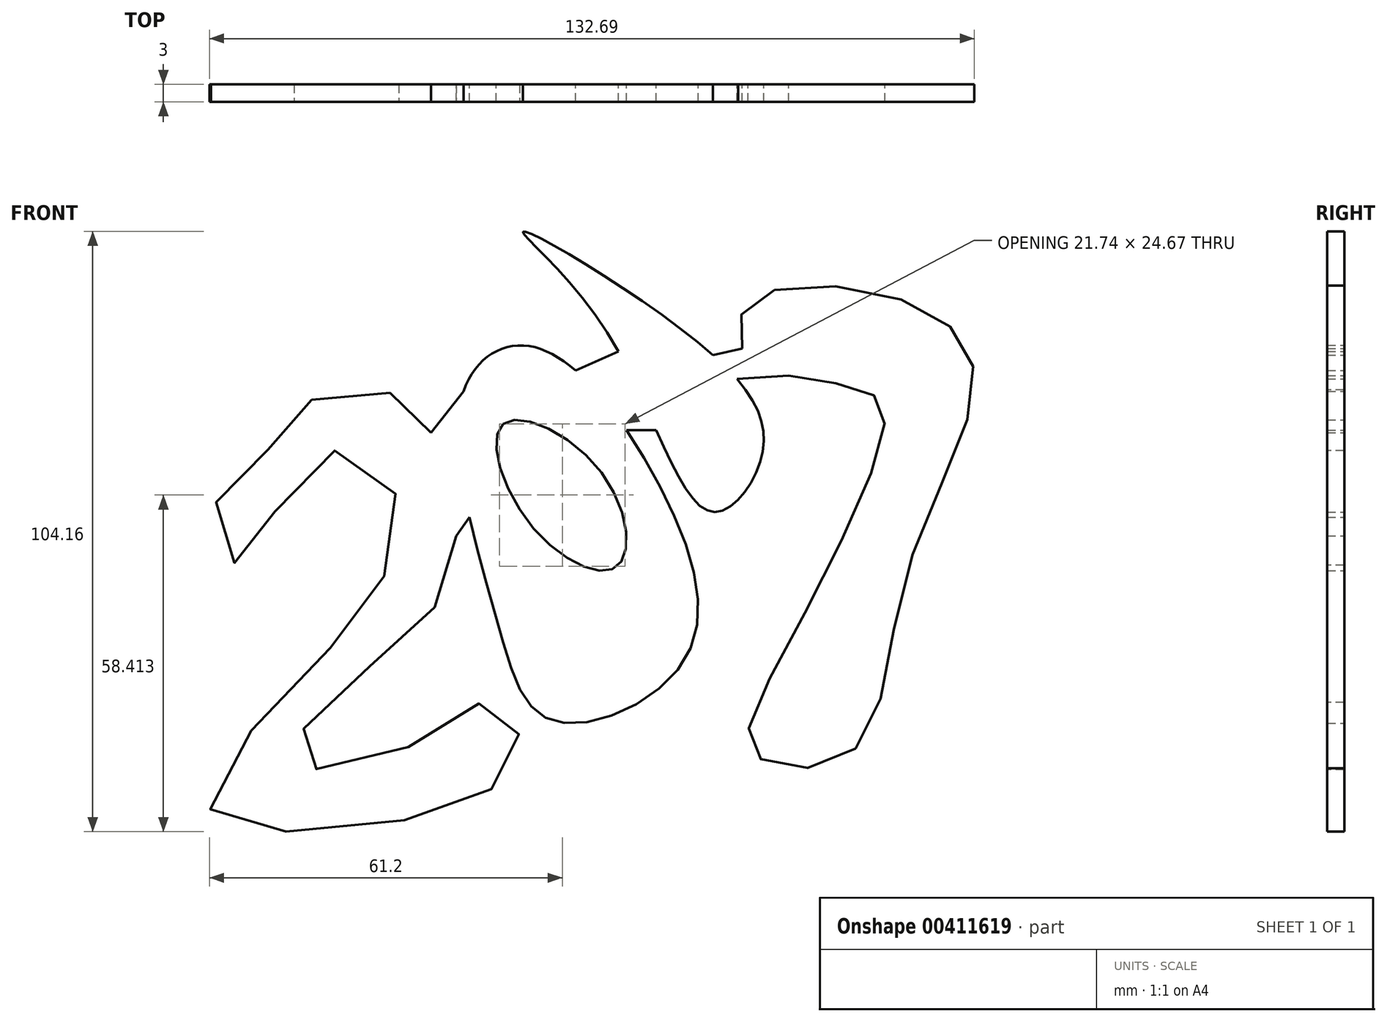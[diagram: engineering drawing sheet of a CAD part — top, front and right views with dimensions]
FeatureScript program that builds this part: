
annotation { "Feature Type Name" : "Feature", "Feature Type Description" : "" }
export const myFeature = defineFeature(function(context is Context, id is Id, definition is map)
    precondition{}
    {
        {
            var Q0;
            Q0=qCreatedBy(makeId("Front.planeOp"),FACE);
            var sketch = newSketch(context, id + "F0", { "sketchPlane" : qUnion([Q0])});
            skFitSpline(sketch, "E0", {"points": [v(-54.59, 23.86) * mm, v(-46.83, 33.4) * mm, v(-31.02, 34.9) * mm, v(-25.06, 28.34) * mm, v(-20.7, 10.42) * mm, v(-25.95, -3.88) * mm, v(-43.55, -18.8) * mm, v(-48.32, -28.64) * mm, v(-30.72, -27.14) * mm, v(-15.21, -18.5) * mm, v(-9.84, -23.86) * mm, v(-14.02, -33.11) * mm, v(-39.97, -40.27) * mm, v(-63.24, -37.29) * mm, v(-48.92, -15.51) * mm, v(-33.11, 3.58) * mm, v(-32.81, 20.88) * mm, v(-47.13, 23.27) * mm, v(-57.27, 5.37) * mm, v(-63.24, 13.42) * mm, v(-54.59, 23.86) * mm]});
            skFitSpline(sketch, "E1", {"points": [v(-19.39, 35.5) * mm, v(-13.72, -3.88) * mm, v(-3.58, -21.78) * mm, v(18.8, -11.34) * mm, v(14.91, 18.5) * mm, v(-7.46, 43.25) * mm, v(-19.39, 35.5) * mm]});
            skFitSpline(sketch, "E2", {"points": [v(-12.53, 29.83) * mm, v(-7.46, 11.93) * mm, v(7.16, 5.07) * mm, v(4.47, 21.48) * mm, v(-12.53, 29.83) * mm]});
            skFitSpline(sketch, "E3", {"points": [v(4.77, 46.83) * mm, v(23.57, 14.62) * mm, v(32.22, 23.86) * mm, v(23.86, 41.76) * mm, v(-8.95, 63.24) * mm, v(4.77, 46.83) * mm]});
            skFitSpline(sketch, "E4", {"points": [v(30.72, 51.3) * mm, v(28.93, 42.95) * mm, v(37, 38.2) * mm, v(51.6, 34.9) * mm, v(53.1, 26.85) * mm, v(35.5, -11.04) * mm, v(31.02, -27.44) * mm, v(47.43, -27.44) * mm, v(57.27, 3.28) * mm, v(69.2, 37.88) * mm, v(57.57, 51) * mm, v(30.72, 51.3) * mm]});
            skLineSegment(sketch, "E5", {"start": v(-25.06, 28.34) * mm, "end": v(-19.39, 35.5) * mm});
            skLineSegment(sketch, "E6", {"start": v(-20.7, 10.42) * mm, "end": v(-18.38, 13.67) * mm});
            skLineSegment(sketch, "E7", {"start": v(0, 39.12) * mm, "end": v(7.45, 42.39) * mm});
            skLineSegment(sketch, "E8", {"start": v(8.85, 28.76) * mm, "end": v(14.03, 28.76) * mm});
            skLineSegment(sketch, "E9", {"start": v(23.86, 41.76) * mm, "end": v(28.93, 42.95) * mm});
            skLineSegment(sketch, "E10", {"start": v(28, 37.62) * mm, "end": v(37, 38.2) * mm});
            skSolve(sketch);
        }
        {
            var Q0;
            Q0 = qSketchRegion(id + "F0", true);
            extrude(context, id + "F1", {"entities" : qUnion([Q0]), "depth" : 3 * mm});
        }
    });
